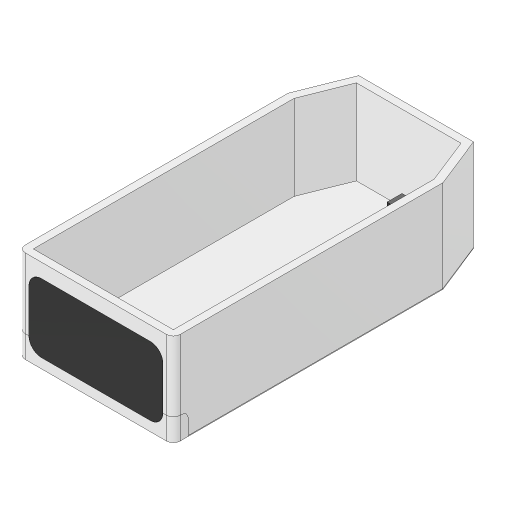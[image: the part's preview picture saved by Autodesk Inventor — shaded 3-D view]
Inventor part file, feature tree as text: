
AUTODESK INVENTOR PART (.ipt)
format: ipt  version: 2024.3 (Build 283343000, 343)  size: 237,056 bytes
history: native  units: mm
features: other x8, extrude x7, sketch x4
ambient origin geometry x8: Origin, YZ Plane, XZ Plane, XY Plane, X Axis, Y Axis, Z Axis, Center Point
bodies: Body1 (feature_tree), Body2 (feature_tree), Body3 (feature_tree), Body4 (feature_tree), Body5 (feature_tree)
feature tree (19):
  other  "實體1"
  sketch  "草圖1"
  extrude  "擠出1"  Depth=15.0mm
  sketch  "草圖2"
  other  "分割1"
  sketch  "草圖3"
  extrude  "擠出2"  Depth=104.0mm
  extrude  "擠出3"  Depth=215.0mm
  extrude  "擠出4"  Depth=107.5mm
  sketch  "草圖4"
  extrude  "擠出5"  Depth=38.217968mm
  extrude  "擠出6"  Depth=12.0mm
  extrude  "擠出7"  Depth=12.66556mm
  other  "Srf1"
  other  "實體4"
  other  "實體5"
  other  "擠出表面1"
  other  "實體2"
  other  "實體3"
